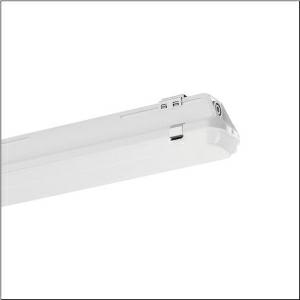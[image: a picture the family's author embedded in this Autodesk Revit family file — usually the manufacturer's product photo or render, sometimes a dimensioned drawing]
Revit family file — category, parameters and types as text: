
# Revit family: monsun_r__12_emergency_51fp10dp468h2_29f9
name_source: partatom
category: Lighting Fixtures
units: mm (PartAtom-declared; Revit-internal decimal feet)

## family parameters
Cut with Voids When Loaded = No
Host = Face
Light Source = No
Part Type = Normal
Room Calculation Point = No
Round Connector Dimension = Use Diameter
Shared = No

## types (1)
- --- (1 x LED, 890 lm, 6.9 W, 4000K)
    Apparent Load = 7 VA
    CIE Flux Codes = 47 77 93 94 100
    Color Rendering = 80
    Color Temperature = 4000K
    Default Elevation = 1800 mm
    Description = Monsun® 12 emergency, damp-proof luminaire, chain hanger, primary optical cover: enclosure, of PMMA, light emission: direct distribution, primary light characteristic: symmetric, installation type: suspended mounting, surface-mounted, horizontal mounting, vertical mounting, LED rated luminous flux: 6.050 lm, light colour: 840, colour temperature: 4000K, control gear: ECG DALI, with terminal, 5-pole, max. 2.5mm², mains connection: 220..240V, AC/DC, 0/50..60Hz, rated input power: 35W, luminaire housing, of glass-fibre reinforced polyester, uncoated, bright grey, length: 1.590 mm, width: 90 mm, height: 88mm, clip for enclosure, of stainless steel (V2A), ceiling mounting element, of stainless steel (V2A), chain hanger, of stainless steel (V2A), protection rating (complete): IP66, insulation class (complete): insulation class I (protective earthing), certification: CE, ENEC, VDE, protection symbol: D, impact resistance: IK04, permissible ambient temperature for indoor applications: -25..+40°C, standard: EN 60598-2-22, EN 50419, EN 60598-2-1, no direct snow, no direct sun, no direct rain, for indoor or canopied outdoor use, corresponds to IFS (International Featured Standards) requirements for safety and quality in the food industry, for animal farming (ammonia tested): for use in cowhouse, pig house, horse-stables... (not for use in poultry stables), AT max for animal farming = 40°C, packaging unit: 1 piece
    Height = 89 mm
    Lamp = 1 x LED
    Lamp Light Flux = 890 lm
    Lamp Power = 6.9 W
    Lamp count = 1
    Length = 1590 mm
    Luminous efficacy = 129 lm/W
    Manufacturer = Siteco
    ModVariant = No
    Model = 51FP10DP468H2
    Mounting Place = Ceiling
    Mounting Type = Pendant
    Number of Poles = 1
    OnlyDefault = Yes
    Power Factor = 1
    Product Name = Monsun® 12 emergency
    Product group = damp-proof luminaire | ceiling pendant
    ProductGroupID = 908
    Protection Class = Protection class I
    Protection Degree = IP 66
    RLX_Detail_Level = 1
    RlxData = <blob elided: 92629 chars, md5=50339a2e>
    Socket = socket
    Standby Power = 0 W
    System Light Flux = 890 lm
    System Power = 7 W
    Type Comments = : equivalent power supply (DC)
    Type Image = l_1004748.jpg
    URL = http://relux.com
    VarID = @adj_125641
    Voltage = 0 V
    Weight = 0.00 kg
    Width = 90 mm

## geometry (parser evidence)
native form markers: Blend x4, Sweep x13
no freeform markers — native parametric forms only
